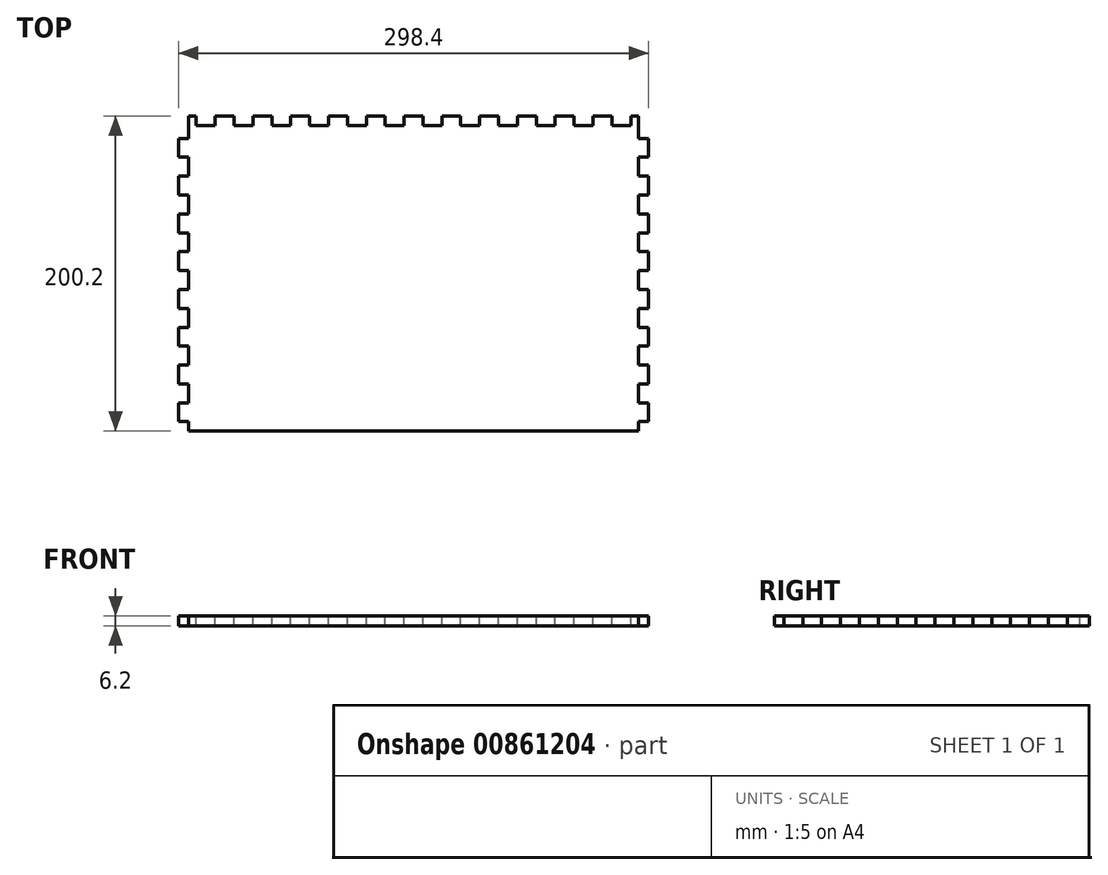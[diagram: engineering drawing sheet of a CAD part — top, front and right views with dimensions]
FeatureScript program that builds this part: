
annotation { "Feature Type Name" : "Feature", "Feature Type Description" : "" }
export const myFeature = defineFeature(function(context is Context, id is Id, definition is map)
    precondition{}
    {
        {
            var Q0;
            Q0=qCreatedBy(makeId("Top.planeOp"),FACE);
            var sketch = newSketch(context, id + "F0", { "sketchPlane" : qUnion([Q0])});
            skLineSegment(sketch, "E0.bottom", {"start": v(143, 110) * mm, "end": v(-143, 110) * mm});
            skLineSegment(sketch, "E0.top", {"start": v(143, -110) * mm, "end": v(-143, -110) * mm});
            skLineSegment(sketch, "E0.left", {"start": v(143, 110) * mm, "end": v(143, -110) * mm});
            skLineSegment(sketch, "E0.right", {"start": v(-143, 110) * mm, "end": v(-143, -110) * mm});
            skPoint(sketch, "E0.middle", {"position": v(0, 0) * mm});
            skSolve(sketch);
        }
        {
            var Q0;
            Q0=qSketchRegion(id+"F0",true);
            extrude(context, id + "F1", {"entities" : qUnion([Q0]), "depth" : 6.2 * mm, "offsetDistance" : 25 * mm});
        }
        {
            var Q0;
            Q0=makeQuery(id+"F1.opExtrude","CAP_FACE",FACE,{"disambiguationData":[OSD([sQuery(id+"F0.wireOp",EDGE,"E0.bottom"),sQuery(id+"F0.wireOp",EDGE,"E0.top"),sQuery(id+"F0.wireOp",EDGE,"E0.left"),sQuery(id+"F0.wireOp",EDGE,"E0.right")])],"isStart":false});
            var sketch = newSketch(context, id + "F2", { "sketchPlane" : qUnion([Q0])});
            skLineSegment(sketch, "E1", {"start": v(0, 110) * mm, "end": v(0, 116.2) * mm, "construction": true});
            skLineSegment(sketch, "E2.bottom", {"start": v(6, 116.2) * mm, "end": v(-6, 116.2) * mm});
            skLineSegment(sketch, "E2.top", {"start": v(6, 110) * mm, "end": v(-6, 110) * mm});
            skLineSegment(sketch, "E2.left", {"start": v(6, 116.2) * mm, "end": v(6, 110) * mm});
            skLineSegment(sketch, "E2.right", {"start": v(-6, 116.2) * mm, "end": v(-6, 110) * mm});
            skPoint(sketch, "E2.middle", {"position": v(0, 113.1) * mm});
            skLineSegment(sketch, "E3.1.0.0", {"start": v(30, 116.2) * mm, "end": v(18, 116.2) * mm});
            skLineSegment(sketch, "E3.1.0.1", {"start": v(30, 116.2) * mm, "end": v(30, 110) * mm});
            skLineSegment(sketch, "E3.1.0.2", {"start": v(18, 116.2) * mm, "end": v(18, 110) * mm});
            skLineSegment(sketch, "E3.1.0.3", {"start": v(30, 110) * mm, "end": v(18, 110) * mm});
            skLineSegment(sketch, "E3.2.0.0", {"start": v(54, 116.2) * mm, "end": v(42, 116.2) * mm});
            skLineSegment(sketch, "E3.2.0.1", {"start": v(54, 116.2) * mm, "end": v(54, 110) * mm});
            skLineSegment(sketch, "E3.2.0.2", {"start": v(42, 116.2) * mm, "end": v(42, 110) * mm});
            skLineSegment(sketch, "E3.2.0.3", {"start": v(54, 110) * mm, "end": v(42, 110) * mm});
            skLineSegment(sketch, "E3.3.0.0", {"start": v(78, 116.2) * mm, "end": v(66, 116.2) * mm});
            skLineSegment(sketch, "E3.3.0.1", {"start": v(78, 116.2) * mm, "end": v(78, 110) * mm});
            skLineSegment(sketch, "E3.3.0.2", {"start": v(66, 116.2) * mm, "end": v(66, 110) * mm});
            skLineSegment(sketch, "E3.3.0.3", {"start": v(78, 110) * mm, "end": v(66, 110) * mm});
            skLineSegment(sketch, "E3.4.0.0", {"start": v(102, 116.2) * mm, "end": v(90, 116.2) * mm});
            skLineSegment(sketch, "E3.4.0.1", {"start": v(102, 116.2) * mm, "end": v(102, 110) * mm});
            skLineSegment(sketch, "E3.4.0.2", {"start": v(90, 116.2) * mm, "end": v(90, 110) * mm});
            skLineSegment(sketch, "E3.4.0.3", {"start": v(102, 110) * mm, "end": v(90, 110) * mm});
            skLineSegment(sketch, "E3.5.0.0", {"start": v(126, 116.2) * mm, "end": v(114, 116.2) * mm});
            skLineSegment(sketch, "E3.5.0.1", {"start": v(126, 116.2) * mm, "end": v(126, 110) * mm});
            skLineSegment(sketch, "E3.5.0.2", {"start": v(114, 116.2) * mm, "end": v(114, 110) * mm});
            skLineSegment(sketch, "E3.5.0.3", {"start": v(126, 110) * mm, "end": v(114, 110) * mm});
            skLineSegment(sketch, "E3.6.0.0", {"start": v(143, 116.2) * mm, "end": v(138, 116.2) * mm});
            skLineSegment(sketch, "E3.6.0.2", {"start": v(138, 116.2) * mm, "end": v(138, 110) * mm});
            skLineSegment(sketch, "E3.6.0.3", {"start": v(143, 110) * mm, "end": v(138, 110) * mm});
            skLineSegment(sketch, "E3.direction1", {"start": v(-6, 116.2) * mm, "end": v(18, 116.2) * mm, "construction": true});
            skLineSegment(sketch, "E4", {"start": v(143, 110) * mm, "end": v(143, 116.2) * mm});
            skPoint(sketch, "E5.orphan", {"position": v(150, 110) * mm});
            skLineSegment(sketch, "E6.MirrorCS", {"start": v(-102, 110) * mm, "end": v(-90, 110) * mm});
            skLineSegment(sketch, "E7.MirrorCS", {"start": v(-143, 116.2) * mm, "end": v(-138, 116.2) * mm});
            skLineSegment(sketch, "E8.MirrorCS", {"start": v(-138, 116.2) * mm, "end": v(-138, 110) * mm});
            skLineSegment(sketch, "E9.MirrorCS", {"start": v(-30, 116.2) * mm, "end": v(-30, 110) * mm});
            skLineSegment(sketch, "E10.MirrorCS", {"start": v(-66, 116.2) * mm, "end": v(-66, 110) * mm});
            skLineSegment(sketch, "E11.MirrorCS", {"start": v(-126, 116.2) * mm, "end": v(-126, 110) * mm});
            skLineSegment(sketch, "E12.MirrorCS", {"start": v(-54, 110) * mm, "end": v(-42, 110) * mm});
            skLineSegment(sketch, "E13.MirrorCS", {"start": v(-143, 110) * mm, "end": v(-143, 116.2) * mm});
            skLineSegment(sketch, "E14.MirrorCS", {"start": v(-54, 116.2) * mm, "end": v(-54, 110) * mm});
            skLineSegment(sketch, "E15.MirrorCS", {"start": v(-114, 116.2) * mm, "end": v(-114, 110) * mm});
            skLineSegment(sketch, "E16.MirrorCS", {"start": v(-102, 116.2) * mm, "end": v(-90, 116.2) * mm});
            skLineSegment(sketch, "E17.MirrorCS", {"start": v(-102, 116.2) * mm, "end": v(-102, 110) * mm});
            skLineSegment(sketch, "E18.MirrorCS", {"start": v(-42, 116.2) * mm, "end": v(-42, 110) * mm});
            skLineSegment(sketch, "E19.MirrorCS", {"start": v(-54, 116.2) * mm, "end": v(-42, 116.2) * mm});
            skLineSegment(sketch, "E20.MirrorCS", {"start": v(-143, 110) * mm, "end": v(-138, 110) * mm});
            skLineSegment(sketch, "E21.MirrorCS", {"start": v(-90, 116.2) * mm, "end": v(-90, 110) * mm});
            skLineSegment(sketch, "E22.MirrorCS", {"start": v(-78, 116.2) * mm, "end": v(-78, 110) * mm});
            skLineSegment(sketch, "E23.MirrorCS", {"start": v(-78, 110) * mm, "end": v(-66, 110) * mm});
            skLineSegment(sketch, "E24.MirrorCS", {"start": v(-126, 116.2) * mm, "end": v(-114, 116.2) * mm});
            skLineSegment(sketch, "E25.MirrorCS", {"start": v(-78, 116.2) * mm, "end": v(-66, 116.2) * mm});
            skLineSegment(sketch, "E26.MirrorCS", {"start": v(-126, 110) * mm, "end": v(-114, 110) * mm});
            skLineSegment(sketch, "E27.MirrorCS", {"start": v(-30, 110) * mm, "end": v(-18, 110) * mm});
            skPoint(sketch, "E28.MirrorP", {"position": v(-150, 110) * mm});
            skLineSegment(sketch, "E29.MirrorCS", {"start": v(-30, 116.2) * mm, "end": v(-18, 116.2) * mm});
            skLineSegment(sketch, "E30.MirrorCS", {"start": v(-18, 116.2) * mm, "end": v(-18, 110) * mm});
            skSolve(sketch);
        }
        {
            var Q0;
            Q0=makeQuery(id+"F2.imprint","IMPRINT",FACE,{"disambiguationData":[TD([[makeQuery(id+"F2.imprint","IMPRINT",EDGE,{"derivedFrom":sQuery(id+"F2.wireOp",EDGE,"E3.6.0.0")}),1.0]])]});
            var Q1;
            Q1=makeQuery(id+"F2.imprint","IMPRINT",FACE,{"disambiguationData":[TD([[makeQuery(id+"F2.imprint","IMPRINT",EDGE,{"derivedFrom":sQuery(id+"F2.wireOp",EDGE,"E3.5.0.0")}),1.0]])]});
            var Q2;
            Q2=makeQuery(id+"F2.imprint","IMPRINT",FACE,{"disambiguationData":[TD([[makeQuery(id+"F2.imprint","IMPRINT",EDGE,{"derivedFrom":sQuery(id+"F2.wireOp",EDGE,"E3.4.0.0")}),1.0]])]});
            var Q3;
            Q3=makeQuery(id+"F2.imprint","IMPRINT",FACE,{"disambiguationData":[TD([[makeQuery(id+"F2.imprint","IMPRINT",EDGE,{"derivedFrom":sQuery(id+"F2.wireOp",EDGE,"E3.3.0.0")}),1.0]])]});
            var Q4;
            Q4=makeQuery(id+"F2.imprint","IMPRINT",FACE,{"disambiguationData":[TD([[makeQuery(id+"F2.imprint","IMPRINT",EDGE,{"derivedFrom":sQuery(id+"F2.wireOp",EDGE,"E3.2.0.0")}),1.0]])]});
            var Q5;
            Q5=makeQuery(id+"F2.imprint","IMPRINT",FACE,{"disambiguationData":[TD([[makeQuery(id+"F2.imprint","IMPRINT",EDGE,{"derivedFrom":sQuery(id+"F2.wireOp",EDGE,"E3.1.0.0")}),1.0]])]});
            var Q6;
            Q6=makeQuery(id+"F2.imprint","IMPRINT",FACE,{"disambiguationData":[TD([[makeQuery(id+"F2.imprint","IMPRINT",EDGE,{"derivedFrom":sQuery(id+"F2.wireOp",EDGE,"E2.bottom")}),1.0]])]});
            var Q7;
            Q7=makeQuery(id+"F2.imprint","IMPRINT",FACE,{"disambiguationData":[TD([[makeQuery(id+"F2.imprint","IMPRINT",EDGE,{"derivedFrom":sQuery(id+"F2.wireOp",EDGE,"E9.MirrorCS")}),1.0]])]});
            var Q8;
            Q8=makeQuery(id+"F2.imprint","IMPRINT",FACE,{"disambiguationData":[TD([[makeQuery(id+"F2.imprint","IMPRINT",EDGE,{"derivedFrom":sQuery(id+"F2.wireOp",EDGE,"E12.MirrorCS")}),-1.0]])]});
            var Q9;
            Q9=makeQuery(id+"F2.imprint","IMPRINT",FACE,{"disambiguationData":[TD([[makeQuery(id+"F2.imprint","IMPRINT",EDGE,{"derivedFrom":sQuery(id+"F2.wireOp",EDGE,"E10.MirrorCS")}),-1.0]])]});
            var Q10;
            Q10=makeQuery(id+"F2.imprint","IMPRINT",FACE,{"disambiguationData":[TD([[makeQuery(id+"F2.imprint","IMPRINT",EDGE,{"derivedFrom":sQuery(id+"F2.wireOp",EDGE,"E6.MirrorCS")}),-1.0]])]});
            var Q11;
            Q11=makeQuery(id+"F2.imprint","IMPRINT",FACE,{"disambiguationData":[TD([[makeQuery(id+"F2.imprint","IMPRINT",EDGE,{"derivedFrom":sQuery(id+"F2.wireOp",EDGE,"E11.MirrorCS")}),1.0]])]});
            var Q12;
            Q12=makeQuery(id+"F2.imprint","IMPRINT",FACE,{"disambiguationData":[TD([[makeQuery(id+"F2.imprint","IMPRINT",EDGE,{"derivedFrom":sQuery(id+"F2.wireOp",EDGE,"E7.MirrorCS")}),-1.0]])]});
            var Q13;
            Q13=makeQuery(id+"F1.opExtrude","CAP_FACE",FACE,{"disambiguationData":[OSD([sQuery(id+"F0.wireOp",EDGE,"E0.bottom"),sQuery(id+"F0.wireOp",EDGE,"E0.top"),sQuery(id+"F0.wireOp",EDGE,"E0.left"),sQuery(id+"F0.wireOp",EDGE,"E0.right")])],"isStart":true});
            extrude(context, id + "F3", {"entities" : qUnion([Q0, Q1, Q2, Q3, Q4, Q5, Q6, Q7, Q8, Q9, Q10, Q11, Q12]), "operationType" : NewBodyOperationType.ADD, "endBound" : BoundingType.UP_TO_SURFACE, "oppositeDirection" : true, "depth" : 25 * mm, "endBoundEntityFace" : qUnion([Q13]), "offsetDistance" : 25 * mm});
        }
        {
            var Q0;
            Q0=makeQuery(id+"F3.boolean.opBoolean","MERGE",FACE,{"derivedFrom":[makeQuery(id+"F1.opExtrude","CAP_FACE",FACE,{"disambiguationData":[OSD([sQuery(id+"F0.wireOp",EDGE,"E0.bottom"),sQuery(id+"F0.wireOp",EDGE,"E0.top"),sQuery(id+"F0.wireOp",EDGE,"E0.left"),sQuery(id+"F0.wireOp",EDGE,"E0.right")])],"isStart":false}),makeQuery(id+"F3.opExtrude","CAP_FACE",FACE,{"disambiguationData":[OSD([sQuery(id+"F2.wireOp",EDGE,"E2.bottom"),sQuery(id+"F2.wireOp",EDGE,"E2.top"),sQuery(id+"F2.wireOp",EDGE,"E2.left"),sQuery(id+"F2.wireOp",EDGE,"E2.right")])],"isStart":true}),makeQuery(id+"F3.opExtrude","CAP_FACE",FACE,{"disambiguationData":[OSD([sQuery(id+"F2.wireOp",EDGE,"E3.1.0.0"),sQuery(id+"F2.wireOp",EDGE,"E3.1.0.1"),sQuery(id+"F2.wireOp",EDGE,"E3.1.0.2"),sQuery(id+"F2.wireOp",EDGE,"E3.1.0.3")])],"isStart":true}),makeQuery(id+"F3.opExtrude","CAP_FACE",FACE,{"disambiguationData":[OSD([sQuery(id+"F2.wireOp",EDGE,"E3.2.0.0"),sQuery(id+"F2.wireOp",EDGE,"E3.2.0.1"),sQuery(id+"F2.wireOp",EDGE,"E3.2.0.2"),sQuery(id+"F2.wireOp",EDGE,"E3.2.0.3")])],"isStart":true}),makeQuery(id+"F3.opExtrude","CAP_FACE",FACE,{"disambiguationData":[OSD([sQuery(id+"F2.wireOp",EDGE,"E3.3.0.0"),sQuery(id+"F2.wireOp",EDGE,"E3.3.0.1"),sQuery(id+"F2.wireOp",EDGE,"E3.3.0.2"),sQuery(id+"F2.wireOp",EDGE,"E3.3.0.3")])],"isStart":true}),makeQuery(id+"F3.opExtrude","CAP_FACE",FACE,{"disambiguationData":[OSD([sQuery(id+"F2.wireOp",EDGE,"E3.4.0.0"),sQuery(id+"F2.wireOp",EDGE,"E3.4.0.1"),sQuery(id+"F2.wireOp",EDGE,"E3.4.0.2"),sQuery(id+"F2.wireOp",EDGE,"E3.4.0.3")])],"isStart":true}),makeQuery(id+"F3.opExtrude","CAP_FACE",FACE,{"disambiguationData":[OSD([sQuery(id+"F2.wireOp",EDGE,"E3.5.0.0"),sQuery(id+"F2.wireOp",EDGE,"E3.5.0.1"),sQuery(id+"F2.wireOp",EDGE,"E3.5.0.2"),sQuery(id+"F2.wireOp",EDGE,"E3.5.0.3")])],"isStart":true}),makeQuery(id+"F3.opExtrude","CAP_FACE",FACE,{"disambiguationData":[OSD([sQuery(id+"F2.wireOp",EDGE,"E3.6.0.0"),sQuery(id+"F2.wireOp",EDGE,"E3.6.0.2"),sQuery(id+"F2.wireOp",EDGE,"E3.6.0.3"),sQuery(id+"F2.wireOp",EDGE,"E4")])],"isStart":true}),makeQuery(id+"F3.opExtrude","CAP_FACE",FACE,{"disambiguationData":[OSD([sQuery(id+"F2.wireOp",EDGE,"E6.MirrorCS"),sQuery(id+"F2.wireOp",EDGE,"E16.MirrorCS"),sQuery(id+"F2.wireOp",EDGE,"E17.MirrorCS"),sQuery(id+"F2.wireOp",EDGE,"E21.MirrorCS")])],"isStart":true}),makeQuery(id+"F3.opExtrude","CAP_FACE",FACE,{"disambiguationData":[OSD([sQuery(id+"F2.wireOp",EDGE,"E7.MirrorCS"),sQuery(id+"F2.wireOp",EDGE,"E8.MirrorCS"),sQuery(id+"F2.wireOp",EDGE,"E13.MirrorCS"),sQuery(id+"F2.wireOp",EDGE,"E20.MirrorCS")])],"isStart":true}),makeQuery(id+"F3.opExtrude","CAP_FACE",FACE,{"disambiguationData":[OSD([sQuery(id+"F2.wireOp",EDGE,"E9.MirrorCS"),sQuery(id+"F2.wireOp",EDGE,"E27.MirrorCS"),sQuery(id+"F2.wireOp",EDGE,"E29.MirrorCS"),sQuery(id+"F2.wireOp",EDGE,"E30.MirrorCS")])],"isStart":true}),makeQuery(id+"F3.opExtrude","CAP_FACE",FACE,{"disambiguationData":[OSD([sQuery(id+"F2.wireOp",EDGE,"E10.MirrorCS"),sQuery(id+"F2.wireOp",EDGE,"E22.MirrorCS"),sQuery(id+"F2.wireOp",EDGE,"E23.MirrorCS"),sQuery(id+"F2.wireOp",EDGE,"E25.MirrorCS")])],"isStart":true}),makeQuery(id+"F3.opExtrude","CAP_FACE",FACE,{"disambiguationData":[OSD([sQuery(id+"F2.wireOp",EDGE,"E11.MirrorCS"),sQuery(id+"F2.wireOp",EDGE,"E15.MirrorCS"),sQuery(id+"F2.wireOp",EDGE,"E24.MirrorCS"),sQuery(id+"F2.wireOp",EDGE,"E26.MirrorCS")])],"isStart":true}),makeQuery(id+"F3.opExtrude","CAP_FACE",FACE,{"disambiguationData":[OSD([sQuery(id+"F2.wireOp",EDGE,"E12.MirrorCS"),sQuery(id+"F2.wireOp",EDGE,"E14.MirrorCS"),sQuery(id+"F2.wireOp",EDGE,"E18.MirrorCS"),sQuery(id+"F2.wireOp",EDGE,"E19.MirrorCS")])],"isStart":true})]});
            var sketch = newSketch(context, id + "F4", { "sketchPlane" : qUnion([Q0])});
            skLineSegment(sketch, "E31", {"start": v(-138, 110) * mm, "end": v(143, 110) * mm, "construction": true});
            skLineSegment(sketch, "E32", {"start": v(0, 0) * mm, "end": v(143, 0) * mm, "construction": true});
            skLineSegment(sketch, "E33", {"start": v(143, 0) * mm, "end": v(149.2, 0) * mm, "construction": true});
            skLineSegment(sketch, "E34.bottom", {"start": v(149.2, 6) * mm, "end": v(143, 6) * mm});
            skLineSegment(sketch, "E34.top", {"start": v(149.2, -6) * mm, "end": v(143, -6) * mm});
            skLineSegment(sketch, "E34.left", {"start": v(149.2, 6) * mm, "end": v(149.2, -6) * mm});
            skLineSegment(sketch, "E34.right", {"start": v(143, 6) * mm, "end": v(143, -6) * mm});
            skPoint(sketch, "E34.middle", {"position": v(146.1, 0) * mm});
            skLineSegment(sketch, "E35.0.1.0", {"start": v(149.2, 30) * mm, "end": v(143, 30) * mm});
            skLineSegment(sketch, "E35.0.1.1", {"start": v(143, 30) * mm, "end": v(143, 18) * mm});
            skLineSegment(sketch, "E35.0.1.2", {"start": v(149.2, 30) * mm, "end": v(149.2, 18) * mm});
            skLineSegment(sketch, "E35.0.1.3", {"start": v(149.2, 18) * mm, "end": v(143, 18) * mm});
            skLineSegment(sketch, "E35.0.2.0", {"start": v(149.2, 54) * mm, "end": v(143, 54) * mm});
            skLineSegment(sketch, "E35.0.2.1", {"start": v(143, 54) * mm, "end": v(143, 42) * mm});
            skLineSegment(sketch, "E35.0.2.2", {"start": v(149.2, 54) * mm, "end": v(149.2, 42) * mm});
            skLineSegment(sketch, "E35.0.2.3", {"start": v(149.2, 42) * mm, "end": v(143, 42) * mm});
            skLineSegment(sketch, "E35.0.3.0", {"start": v(149.2, 78) * mm, "end": v(143, 78) * mm});
            skLineSegment(sketch, "E35.0.3.1", {"start": v(143, 78) * mm, "end": v(143, 66) * mm});
            skLineSegment(sketch, "E35.0.3.2", {"start": v(149.2, 78) * mm, "end": v(149.2, 66) * mm});
            skLineSegment(sketch, "E35.0.3.3", {"start": v(149.2, 66) * mm, "end": v(143, 66) * mm});
            skLineSegment(sketch, "E35.0.4.0", {"start": v(149.2, 102) * mm, "end": v(143, 102) * mm});
            skLineSegment(sketch, "E35.0.4.1", {"start": v(143, 102) * mm, "end": v(143, 90) * mm});
            skLineSegment(sketch, "E35.0.4.2", {"start": v(149.2, 102) * mm, "end": v(149.2, 90) * mm});
            skLineSegment(sketch, "E35.0.4.3", {"start": v(149.2, 90) * mm, "end": v(143, 90) * mm});
            skLineSegment(sketch, "E35.direction1", {"start": v(143, 6) * mm, "end": v(168, 6) * mm, "construction": true});
            skLineSegment(sketch, "E35.direction2", {"start": v(143, 6) * mm, "end": v(143, 30) * mm, "construction": true});
            skLineSegment(sketch, "E36.MirrorCS", {"start": v(143, -30) * mm, "end": v(143, -18) * mm});
            skLineSegment(sketch, "E37.MirrorCS", {"start": v(149.2, -78) * mm, "end": v(149.2, -66) * mm});
            skLineSegment(sketch, "E38.MirrorCS", {"start": v(149.2, -66) * mm, "end": v(143, -66) * mm});
            skLineSegment(sketch, "E39.MirrorCS", {"start": v(149.2, -102) * mm, "end": v(143, -102) * mm});
            skLineSegment(sketch, "E40.MirrorCS", {"start": v(143, -102) * mm, "end": v(143, -90) * mm});
            skLineSegment(sketch, "E41.MirrorCS", {"start": v(149.2, -102) * mm, "end": v(149.2, -90) * mm});
            skLineSegment(sketch, "E42.MirrorCS", {"start": v(149.2, -90) * mm, "end": v(143, -90) * mm});
            skLineSegment(sketch, "E43.MirrorCS", {"start": v(143, -6) * mm, "end": v(143, -30) * mm, "construction": true});
            skLineSegment(sketch, "E44.MirrorCS", {"start": v(143, -54) * mm, "end": v(143, -42) * mm});
            skLineSegment(sketch, "E45.MirrorCS", {"start": v(149.2, -42) * mm, "end": v(143, -42) * mm});
            skLineSegment(sketch, "E46.MirrorCS", {"start": v(149.2, -54) * mm, "end": v(143, -54) * mm});
            skLineSegment(sketch, "E47.MirrorCS", {"start": v(149.2, -54) * mm, "end": v(149.2, -42) * mm});
            skLineSegment(sketch, "E48.MirrorCS", {"start": v(149.2, -18) * mm, "end": v(143, -18) * mm});
            skLineSegment(sketch, "E49.MirrorCS", {"start": v(143, -78) * mm, "end": v(143, -66) * mm});
            skLineSegment(sketch, "E50.MirrorCS", {"start": v(149.2, -78) * mm, "end": v(143, -78) * mm});
            skLineSegment(sketch, "E51.MirrorCS", {"start": v(149.2, -30) * mm, "end": v(143, -30) * mm});
            skLineSegment(sketch, "E52.MirrorCS", {"start": v(149.2, -30) * mm, "end": v(149.2, -18) * mm});
            skLineSegment(sketch, "E53.MirrorCS", {"start": v(-143, 6) * mm, "end": v(-143, -6) * mm});
            skLineSegment(sketch, "E54.MirrorCS", {"start": v(-149.2, 6) * mm, "end": v(-149.2, -6) * mm});
            skLineSegment(sketch, "E55.MirrorCS", {"start": v(-149.2, -6) * mm, "end": v(-143, -6) * mm});
            skLineSegment(sketch, "E56.MirrorCS", {"start": v(-149.2, 6) * mm, "end": v(-143, 6) * mm});
            skLineSegment(sketch, "E57.MirrorCS", {"start": v(-143, 0) * mm, "end": v(-149.2, 0) * mm, "construction": true});
            skLineSegment(sketch, "E58.MirrorCS", {"start": v(-143, 30) * mm, "end": v(-143, 18) * mm});
            skLineSegment(sketch, "E59.MirrorCS", {"start": v(-149.2, -30) * mm, "end": v(-143, -30) * mm});
            skLineSegment(sketch, "E60.MirrorCS", {"start": v(-143, -30) * mm, "end": v(-143, -18) * mm});
            skLineSegment(sketch, "E61.MirrorCS", {"start": v(-149.2, 30) * mm, "end": v(-143, 30) * mm});
            skLineSegment(sketch, "E62.MirrorCS", {"start": v(-149.2, 78) * mm, "end": v(-149.2, 66) * mm});
            skLineSegment(sketch, "E63.MirrorCS", {"start": v(-143, -54) * mm, "end": v(-143, -42) * mm});
            skLineSegment(sketch, "E64.MirrorCS", {"start": v(-149.2, 66) * mm, "end": v(-143, 66) * mm});
            skLineSegment(sketch, "E65.MirrorCS", {"start": v(-149.2, -42) * mm, "end": v(-143, -42) * mm});
            skLineSegment(sketch, "E66.MirrorCS", {"start": v(-149.2, 102) * mm, "end": v(-143, 102) * mm});
            skLineSegment(sketch, "E67.MirrorCS", {"start": v(-149.2, -54) * mm, "end": v(-143, -54) * mm});
            skLineSegment(sketch, "E68.MirrorCS", {"start": v(-149.2, -90) * mm, "end": v(-143, -90) * mm});
            skLineSegment(sketch, "E69.MirrorCS", {"start": v(-143, 102) * mm, "end": v(-143, 90) * mm});
            skLineSegment(sketch, "E70.MirrorCS", {"start": v(-149.2, -54) * mm, "end": v(-149.2, -42) * mm});
            skLineSegment(sketch, "E71.MirrorCS", {"start": v(-143, -102) * mm, "end": v(-143, -90) * mm});
            skLineSegment(sketch, "E72.MirrorCS", {"start": v(-149.2, 102) * mm, "end": v(-149.2, 90) * mm});
            skLineSegment(sketch, "E73.MirrorCS", {"start": v(-149.2, -18) * mm, "end": v(-143, -18) * mm});
            skLineSegment(sketch, "E74.MirrorCS", {"start": v(-149.2, -102) * mm, "end": v(-149.2, -90) * mm});
            skLineSegment(sketch, "E75.MirrorCS", {"start": v(-143, 78) * mm, "end": v(-143, 66) * mm});
            skLineSegment(sketch, "E76.MirrorCS", {"start": v(-149.2, 18) * mm, "end": v(-143, 18) * mm});
            skLineSegment(sketch, "E77.MirrorCS", {"start": v(-149.2, 42) * mm, "end": v(-143, 42) * mm});
            skLineSegment(sketch, "E78.MirrorCS", {"start": v(-149.2, -102) * mm, "end": v(-143, -102) * mm});
            skLineSegment(sketch, "E79.MirrorCS", {"start": v(-149.2, 30) * mm, "end": v(-149.2, 18) * mm});
            skLineSegment(sketch, "E80.MirrorCS", {"start": v(-149.2, -66) * mm, "end": v(-143, -66) * mm});
            skLineSegment(sketch, "E81.MirrorCS", {"start": v(-149.2, 54) * mm, "end": v(-149.2, 42) * mm});
            skLineSegment(sketch, "E82.MirrorCS", {"start": v(-149.2, -78) * mm, "end": v(-149.2, -66) * mm});
            skLineSegment(sketch, "E83.MirrorCS", {"start": v(-143, -78) * mm, "end": v(-143, -66) * mm});
            skLineSegment(sketch, "E84.MirrorCS", {"start": v(-149.2, -30) * mm, "end": v(-149.2, -18) * mm});
            skLineSegment(sketch, "E85.MirrorCS", {"start": v(-149.2, 54) * mm, "end": v(-143, 54) * mm});
            skLineSegment(sketch, "E86.MirrorCS", {"start": v(-143, -6) * mm, "end": v(-143, -30) * mm, "construction": true});
            skLineSegment(sketch, "E87.MirrorCS", {"start": v(-143, 54) * mm, "end": v(-143, 42) * mm});
            skLineSegment(sketch, "E88.MirrorCS", {"start": v(-143, 6) * mm, "end": v(-143, 30) * mm, "construction": true});
            skLineSegment(sketch, "E89.MirrorCS", {"start": v(-149.2, 78) * mm, "end": v(-143, 78) * mm});
            skLineSegment(sketch, "E90.MirrorCS", {"start": v(-149.2, -78) * mm, "end": v(-143, -78) * mm});
            skLineSegment(sketch, "E91.MirrorCS", {"start": v(-149.2, 90) * mm, "end": v(-143, 90) * mm});
            skLineSegment(sketch, "E92.MirrorCS", {"start": v(-143, 6) * mm, "end": v(-168, 6) * mm, "construction": true});
            skPoint(sketch, "E93.MirrorP", {"position": v(-146.1, 0) * mm});
            skSolve(sketch);
        }
        {
            var Q0;
            Q0=makeQuery(id+"F4.imprint","IMPRINT",FACE,{"disambiguationData":[TD([[makeQuery(id+"F4.imprint","IMPRINT",EDGE,{"derivedFrom":sQuery(id+"F4.wireOp",EDGE,"E39.MirrorCS")}),-1.0]])]});
            var Q1;
            Q1=makeQuery(id+"F4.imprint","IMPRINT",FACE,{"disambiguationData":[TD([[makeQuery(id+"F4.imprint","IMPRINT",EDGE,{"derivedFrom":sQuery(id+"F4.wireOp",EDGE,"E37.MirrorCS")}),1.0]])]});
            var Q2;
            Q2=makeQuery(id+"F4.imprint","IMPRINT",FACE,{"disambiguationData":[TD([[makeQuery(id+"F4.imprint","IMPRINT",EDGE,{"derivedFrom":sQuery(id+"F4.wireOp",EDGE,"E44.MirrorCS")}),1.0]])]});
            var Q3;
            Q3=makeQuery(id+"F4.imprint","IMPRINT",FACE,{"disambiguationData":[TD([[makeQuery(id+"F4.imprint","IMPRINT",EDGE,{"derivedFrom":sQuery(id+"F4.wireOp",EDGE,"E36.MirrorCS")}),1.0]])]});
            var Q4;
            Q4=makeQuery(id+"F4.imprint","IMPRINT",FACE,{"disambiguationData":[TD([[makeQuery(id+"F4.imprint","IMPRINT",EDGE,{"derivedFrom":sQuery(id+"F4.wireOp",EDGE,"E34.bottom")}),1.0]])]});
            var Q5;
            Q5=makeQuery(id+"F4.imprint","IMPRINT",FACE,{"disambiguationData":[TD([[makeQuery(id+"F4.imprint","IMPRINT",EDGE,{"derivedFrom":sQuery(id+"F4.wireOp",EDGE,"E35.0.1.0")}),1.0]])]});
            var Q6;
            Q6=makeQuery(id+"F4.imprint","IMPRINT",FACE,{"disambiguationData":[TD([[makeQuery(id+"F4.imprint","IMPRINT",EDGE,{"derivedFrom":sQuery(id+"F4.wireOp",EDGE,"E35.0.2.0")}),1.0]])]});
            var Q7;
            Q7=makeQuery(id+"F4.imprint","IMPRINT",FACE,{"disambiguationData":[TD([[makeQuery(id+"F4.imprint","IMPRINT",EDGE,{"derivedFrom":sQuery(id+"F4.wireOp",EDGE,"E35.0.3.0")}),1.0]])]});
            var Q8;
            Q8=makeQuery(id+"F4.imprint","IMPRINT",FACE,{"disambiguationData":[TD([[makeQuery(id+"F4.imprint","IMPRINT",EDGE,{"derivedFrom":sQuery(id+"F4.wireOp",EDGE,"E35.0.4.0")}),1.0]])]});
            var Q9;
            Q9=makeQuery(id+"F4.imprint","IMPRINT",FACE,{"disambiguationData":[TD([[makeQuery(id+"F4.imprint","IMPRINT",EDGE,{"derivedFrom":sQuery(id+"F4.wireOp",EDGE,"E66.MirrorCS")}),-1.0]])]});
            var Q10;
            Q10=makeQuery(id+"F4.imprint","IMPRINT",FACE,{"disambiguationData":[TD([[makeQuery(id+"F4.imprint","IMPRINT",EDGE,{"derivedFrom":sQuery(id+"F4.wireOp",EDGE,"E62.MirrorCS")}),1.0]])]});
            var Q11;
            Q11=makeQuery(id+"F4.imprint","IMPRINT",FACE,{"disambiguationData":[TD([[makeQuery(id+"F4.imprint","IMPRINT",EDGE,{"derivedFrom":sQuery(id+"F4.wireOp",EDGE,"E77.MirrorCS")}),1.0]])]});
            var Q12;
            Q12=makeQuery(id+"F4.imprint","IMPRINT",FACE,{"disambiguationData":[TD([[makeQuery(id+"F4.imprint","IMPRINT",EDGE,{"derivedFrom":sQuery(id+"F4.wireOp",EDGE,"E58.MirrorCS")}),-1.0]])]});
            var Q13;
            Q13=makeQuery(id+"F4.imprint","IMPRINT",FACE,{"disambiguationData":[TD([[makeQuery(id+"F4.imprint","IMPRINT",EDGE,{"derivedFrom":sQuery(id+"F4.wireOp",EDGE,"E53.MirrorCS")}),-1.0]])]});
            var Q14;
            Q14=makeQuery(id+"F4.imprint","IMPRINT",FACE,{"disambiguationData":[TD([[makeQuery(id+"F4.imprint","IMPRINT",EDGE,{"derivedFrom":sQuery(id+"F4.wireOp",EDGE,"E59.MirrorCS")}),1.0]])]});
            var Q15;
            Q15=makeQuery(id+"F4.imprint","IMPRINT",FACE,{"disambiguationData":[TD([[makeQuery(id+"F4.imprint","IMPRINT",EDGE,{"derivedFrom":sQuery(id+"F4.wireOp",EDGE,"E63.MirrorCS")}),-1.0]])]});
            var Q16;
            Q16=makeQuery(id+"F4.imprint","IMPRINT",FACE,{"disambiguationData":[TD([[makeQuery(id+"F4.imprint","IMPRINT",EDGE,{"derivedFrom":sQuery(id+"F4.wireOp",EDGE,"E80.MirrorCS")}),-1.0]])]});
            var Q17;
            Q17=makeQuery(id+"F4.imprint","IMPRINT",FACE,{"disambiguationData":[TD([[makeQuery(id+"F4.imprint","IMPRINT",EDGE,{"derivedFrom":sQuery(id+"F4.wireOp",EDGE,"E68.MirrorCS")}),-1.0]])]});
            var Q18;
            {var subQ0=sQuery(id+"F0.wireOp",EDGE,"E0.right");var subQ1=sQuery(id+"F0.wireOp",EDGE,"E0.left");var subQ2=sQuery(id+"F0.wireOp",EDGE,"E0.top");var subQ3=sQuery(id+"F0.wireOp",EDGE,"E0.bottom");Q18=makeQuery(id+"F3.boolean.opBoolean","MERGE",FACE,{"derivedFrom":[makeQuery(id+"F1.opExtrude","CAP_FACE",FACE,{"disambiguationData":[OSD([subQ3,subQ2,subQ1,subQ0])],"isStart":true}),makeQuery(id+"F3.opExtrude","CAP_FACE",FACE,{"disambiguationData":[OSD([subQ3,subQ2,subQ1,subQ0]),OD(0.0)],"isStart":false}),makeQuery(id+"F3.opExtrude","CAP_FACE",FACE,{"disambiguationData":[OSD([subQ3,subQ2,subQ1,subQ0]),OD(1.0)],"isStart":false}),makeQuery(id+"F3.opExtrude","CAP_FACE",FACE,{"disambiguationData":[OSD([subQ3,subQ2,subQ1,subQ0]),OD(2.0)],"isStart":false}),makeQuery(id+"F3.opExtrude","CAP_FACE",FACE,{"disambiguationData":[OSD([subQ3,subQ2,subQ1,subQ0]),OD(3.0)],"isStart":false}),makeQuery(id+"F3.opExtrude","CAP_FACE",FACE,{"disambiguationData":[OSD([subQ3,subQ2,subQ1,subQ0]),OD(4.0)],"isStart":false}),makeQuery(id+"F3.opExtrude","CAP_FACE",FACE,{"disambiguationData":[OSD([subQ3,subQ2,subQ1,subQ0]),OD(5.0)],"isStart":false}),makeQuery(id+"F3.opExtrude","CAP_FACE",FACE,{"disambiguationData":[OSD([subQ3,subQ2,subQ1,subQ0]),OD(6.0)],"isStart":false}),makeQuery(id+"F3.opExtrude","CAP_FACE",FACE,{"disambiguationData":[OSD([subQ3,subQ2,subQ1,subQ0]),OD(7.0)],"isStart":false}),makeQuery(id+"F3.opExtrude","CAP_FACE",FACE,{"disambiguationData":[OSD([subQ3,subQ2,subQ1,subQ0]),OD(8.0)],"isStart":false}),makeQuery(id+"F3.opExtrude","CAP_FACE",FACE,{"disambiguationData":[OSD([subQ3,subQ2,subQ1,subQ0]),OD(9.0)],"isStart":false}),makeQuery(id+"F3.opExtrude","CAP_FACE",FACE,{"disambiguationData":[OSD([subQ3,subQ2,subQ1,subQ0]),OD(10.0)],"isStart":false}),makeQuery(id+"F3.opExtrude","CAP_FACE",FACE,{"disambiguationData":[OSD([subQ3,subQ2,subQ1,subQ0]),OD(11.0)],"isStart":false}),makeQuery(id+"F3.opExtrude","CAP_FACE",FACE,{"disambiguationData":[OSD([subQ3,subQ2,subQ1,subQ0]),OD(12.0)],"isStart":false})]});}
            extrude(context, id + "F5", {"entities" : qUnion([Q0, Q1, Q2, Q3, Q4, Q5, Q6, Q7, Q8, Q9, Q10, Q11, Q12, Q13, Q14, Q15, Q16, Q17]), "operationType" : NewBodyOperationType.ADD, "endBound" : BoundingType.UP_TO_SURFACE, "oppositeDirection" : true, "depth" : 25 * mm, "endBoundEntityFace" : qUnion([Q18]), "offsetDistance" : 25 * mm});
        }
        {
            var Q0;
            Q0=makeQuery(id+"F5.boolean.opBoolean","MERGE",FACE,{"derivedFrom":[makeQuery(id+"F3.boolean.opBoolean","MERGE",FACE,{"derivedFrom":[makeQuery(id+"F1.opExtrude","CAP_FACE",FACE,{"disambiguationData":[OSD([sQuery(id+"F0.wireOp",EDGE,"E0.bottom"),sQuery(id+"F0.wireOp",EDGE,"E0.top"),sQuery(id+"F0.wireOp",EDGE,"E0.left"),sQuery(id+"F0.wireOp",EDGE,"E0.right")])],"isStart":false}),makeQuery(id+"F3.opExtrude","CAP_FACE",FACE,{"disambiguationData":[OSD([sQuery(id+"F2.wireOp",EDGE,"E2.bottom"),sQuery(id+"F2.wireOp",EDGE,"E2.top"),sQuery(id+"F2.wireOp",EDGE,"E2.left"),sQuery(id+"F2.wireOp",EDGE,"E2.right")])],"isStart":true}),makeQuery(id+"F3.opExtrude","CAP_FACE",FACE,{"disambiguationData":[OSD([sQuery(id+"F2.wireOp",EDGE,"E3.1.0.0"),sQuery(id+"F2.wireOp",EDGE,"E3.1.0.1"),sQuery(id+"F2.wireOp",EDGE,"E3.1.0.2"),sQuery(id+"F2.wireOp",EDGE,"E3.1.0.3")])],"isStart":true}),makeQuery(id+"F3.opExtrude","CAP_FACE",FACE,{"disambiguationData":[OSD([sQuery(id+"F2.wireOp",EDGE,"E3.2.0.0"),sQuery(id+"F2.wireOp",EDGE,"E3.2.0.1"),sQuery(id+"F2.wireOp",EDGE,"E3.2.0.2"),sQuery(id+"F2.wireOp",EDGE,"E3.2.0.3")])],"isStart":true}),makeQuery(id+"F3.opExtrude","CAP_FACE",FACE,{"disambiguationData":[OSD([sQuery(id+"F2.wireOp",EDGE,"E3.3.0.0"),sQuery(id+"F2.wireOp",EDGE,"E3.3.0.1"),sQuery(id+"F2.wireOp",EDGE,"E3.3.0.2"),sQuery(id+"F2.wireOp",EDGE,"E3.3.0.3")])],"isStart":true}),makeQuery(id+"F3.opExtrude","CAP_FACE",FACE,{"disambiguationData":[OSD([sQuery(id+"F2.wireOp",EDGE,"E3.4.0.0"),sQuery(id+"F2.wireOp",EDGE,"E3.4.0.1"),sQuery(id+"F2.wireOp",EDGE,"E3.4.0.2"),sQuery(id+"F2.wireOp",EDGE,"E3.4.0.3")])],"isStart":true}),makeQuery(id+"F3.opExtrude","CAP_FACE",FACE,{"disambiguationData":[OSD([sQuery(id+"F2.wireOp",EDGE,"E3.5.0.0"),sQuery(id+"F2.wireOp",EDGE,"E3.5.0.1"),sQuery(id+"F2.wireOp",EDGE,"E3.5.0.2"),sQuery(id+"F2.wireOp",EDGE,"E3.5.0.3")])],"isStart":true}),makeQuery(id+"F3.opExtrude","CAP_FACE",FACE,{"disambiguationData":[OSD([sQuery(id+"F2.wireOp",EDGE,"E3.6.0.0"),sQuery(id+"F2.wireOp",EDGE,"E3.6.0.2"),sQuery(id+"F2.wireOp",EDGE,"E3.6.0.3"),sQuery(id+"F2.wireOp",EDGE,"E4")])],"isStart":true}),makeQuery(id+"F3.opExtrude","CAP_FACE",FACE,{"disambiguationData":[OSD([sQuery(id+"F2.wireOp",EDGE,"E6.MirrorCS"),sQuery(id+"F2.wireOp",EDGE,"E16.MirrorCS"),sQuery(id+"F2.wireOp",EDGE,"E17.MirrorCS"),sQuery(id+"F2.wireOp",EDGE,"E21.MirrorCS")])],"isStart":true}),makeQuery(id+"F3.opExtrude","CAP_FACE",FACE,{"disambiguationData":[OSD([sQuery(id+"F2.wireOp",EDGE,"E7.MirrorCS"),sQuery(id+"F2.wireOp",EDGE,"E8.MirrorCS"),sQuery(id+"F2.wireOp",EDGE,"E13.MirrorCS"),sQuery(id+"F2.wireOp",EDGE,"E20.MirrorCS")])],"isStart":true}),makeQuery(id+"F3.opExtrude","CAP_FACE",FACE,{"disambiguationData":[OSD([sQuery(id+"F2.wireOp",EDGE,"E9.MirrorCS"),sQuery(id+"F2.wireOp",EDGE,"E27.MirrorCS"),sQuery(id+"F2.wireOp",EDGE,"E29.MirrorCS"),sQuery(id+"F2.wireOp",EDGE,"E30.MirrorCS")])],"isStart":true}),makeQuery(id+"F3.opExtrude","CAP_FACE",FACE,{"disambiguationData":[OSD([sQuery(id+"F2.wireOp",EDGE,"E10.MirrorCS"),sQuery(id+"F2.wireOp",EDGE,"E22.MirrorCS"),sQuery(id+"F2.wireOp",EDGE,"E23.MirrorCS"),sQuery(id+"F2.wireOp",EDGE,"E25.MirrorCS")])],"isStart":true}),makeQuery(id+"F3.opExtrude","CAP_FACE",FACE,{"disambiguationData":[OSD([sQuery(id+"F2.wireOp",EDGE,"E11.MirrorCS"),sQuery(id+"F2.wireOp",EDGE,"E15.MirrorCS"),sQuery(id+"F2.wireOp",EDGE,"E24.MirrorCS"),sQuery(id+"F2.wireOp",EDGE,"E26.MirrorCS")])],"isStart":true}),makeQuery(id+"F3.opExtrude","CAP_FACE",FACE,{"disambiguationData":[OSD([sQuery(id+"F2.wireOp",EDGE,"E12.MirrorCS"),sQuery(id+"F2.wireOp",EDGE,"E14.MirrorCS"),sQuery(id+"F2.wireOp",EDGE,"E18.MirrorCS"),sQuery(id+"F2.wireOp",EDGE,"E19.MirrorCS")])],"isStart":true})]}),makeQuery(id+"F5.opExtrude","CAP_FACE",FACE,{"disambiguationData":[OSD([sQuery(id+"F4.wireOp",EDGE,"E34.bottom"),sQuery(id+"F4.wireOp",EDGE,"E34.top"),sQuery(id+"F4.wireOp",EDGE,"E34.left"),sQuery(id+"F4.wireOp",EDGE,"E34.right")])],"isStart":true}),makeQuery(id+"F5.opExtrude","CAP_FACE",FACE,{"disambiguationData":[OSD([sQuery(id+"F4.wireOp",EDGE,"E35.0.1.0"),sQuery(id+"F4.wireOp",EDGE,"E35.0.1.1"),sQuery(id+"F4.wireOp",EDGE,"E35.0.1.2"),sQuery(id+"F4.wireOp",EDGE,"E35.0.1.3")])],"isStart":true}),makeQuery(id+"F5.opExtrude","CAP_FACE",FACE,{"disambiguationData":[OSD([sQuery(id+"F4.wireOp",EDGE,"E35.0.2.0"),sQuery(id+"F4.wireOp",EDGE,"E35.0.2.1"),sQuery(id+"F4.wireOp",EDGE,"E35.0.2.2"),sQuery(id+"F4.wireOp",EDGE,"E35.0.2.3")])],"isStart":true}),makeQuery(id+"F5.opExtrude","CAP_FACE",FACE,{"disambiguationData":[OSD([sQuery(id+"F4.wireOp",EDGE,"E35.0.3.0"),sQuery(id+"F4.wireOp",EDGE,"E35.0.3.1"),sQuery(id+"F4.wireOp",EDGE,"E35.0.3.2"),sQuery(id+"F4.wireOp",EDGE,"E35.0.3.3")])],"isStart":true}),makeQuery(id+"F5.opExtrude","CAP_FACE",FACE,{"disambiguationData":[OSD([sQuery(id+"F4.wireOp",EDGE,"E35.0.4.0"),sQuery(id+"F4.wireOp",EDGE,"E35.0.4.1"),sQuery(id+"F4.wireOp",EDGE,"E35.0.4.2"),sQuery(id+"F4.wireOp",EDGE,"E35.0.4.3")])],"isStart":true}),makeQuery(id+"F5.opExtrude","CAP_FACE",FACE,{"disambiguationData":[OSD([sQuery(id+"F4.wireOp",EDGE,"E36.MirrorCS"),sQuery(id+"F4.wireOp",EDGE,"E48.MirrorCS"),sQuery(id+"F4.wireOp",EDGE,"E51.MirrorCS"),sQuery(id+"F4.wireOp",EDGE,"E52.MirrorCS")])],"isStart":true}),makeQuery(id+"F5.opExtrude","CAP_FACE",FACE,{"disambiguationData":[OSD([sQuery(id+"F4.wireOp",EDGE,"E37.MirrorCS"),sQuery(id+"F4.wireOp",EDGE,"E38.MirrorCS"),sQuery(id+"F4.wireOp",EDGE,"E49.MirrorCS"),sQuery(id+"F4.wireOp",EDGE,"E50.MirrorCS")])],"isStart":true}),makeQuery(id+"F5.opExtrude","CAP_FACE",FACE,{"disambiguationData":[OSD([sQuery(id+"F4.wireOp",EDGE,"E39.MirrorCS"),sQuery(id+"F4.wireOp",EDGE,"E40.MirrorCS"),sQuery(id+"F4.wireOp",EDGE,"E41.MirrorCS"),sQuery(id+"F4.wireOp",EDGE,"E42.MirrorCS")])],"isStart":true}),makeQuery(id+"F5.opExtrude","CAP_FACE",FACE,{"disambiguationData":[OSD([sQuery(id+"F4.wireOp",EDGE,"E44.MirrorCS"),sQuery(id+"F4.wireOp",EDGE,"E45.MirrorCS"),sQuery(id+"F4.wireOp",EDGE,"E46.MirrorCS"),sQuery(id+"F4.wireOp",EDGE,"E47.MirrorCS")])],"isStart":true}),makeQuery(id+"F5.opExtrude","CAP_FACE",FACE,{"disambiguationData":[OSD([sQuery(id+"F4.wireOp",EDGE,"E53.MirrorCS"),sQuery(id+"F4.wireOp",EDGE,"E54.MirrorCS"),sQuery(id+"F4.wireOp",EDGE,"E55.MirrorCS"),sQuery(id+"F4.wireOp",EDGE,"E56.MirrorCS")])],"isStart":true}),makeQuery(id+"F5.opExtrude","CAP_FACE",FACE,{"disambiguationData":[OSD([sQuery(id+"F4.wireOp",EDGE,"E58.MirrorCS"),sQuery(id+"F4.wireOp",EDGE,"E61.MirrorCS"),sQuery(id+"F4.wireOp",EDGE,"E76.MirrorCS"),sQuery(id+"F4.wireOp",EDGE,"E79.MirrorCS")])],"isStart":true}),makeQuery(id+"F5.opExtrude","CAP_FACE",FACE,{"disambiguationData":[OSD([sQuery(id+"F4.wireOp",EDGE,"E59.MirrorCS"),sQuery(id+"F4.wireOp",EDGE,"E60.MirrorCS"),sQuery(id+"F4.wireOp",EDGE,"E73.MirrorCS"),sQuery(id+"F4.wireOp",EDGE,"E84.MirrorCS")])],"isStart":true}),makeQuery(id+"F5.opExtrude","CAP_FACE",FACE,{"disambiguationData":[OSD([sQuery(id+"F4.wireOp",EDGE,"E62.MirrorCS"),sQuery(id+"F4.wireOp",EDGE,"E64.MirrorCS"),sQuery(id+"F4.wireOp",EDGE,"E75.MirrorCS"),sQuery(id+"F4.wireOp",EDGE,"E89.MirrorCS")])],"isStart":true}),makeQuery(id+"F5.opExtrude","CAP_FACE",FACE,{"disambiguationData":[OSD([sQuery(id+"F4.wireOp",EDGE,"E63.MirrorCS"),sQuery(id+"F4.wireOp",EDGE,"E65.MirrorCS"),sQuery(id+"F4.wireOp",EDGE,"E67.MirrorCS"),sQuery(id+"F4.wireOp",EDGE,"E70.MirrorCS")])],"isStart":true}),makeQuery(id+"F5.opExtrude","CAP_FACE",FACE,{"disambiguationData":[OSD([sQuery(id+"F4.wireOp",EDGE,"E66.MirrorCS"),sQuery(id+"F4.wireOp",EDGE,"E69.MirrorCS"),sQuery(id+"F4.wireOp",EDGE,"E72.MirrorCS"),sQuery(id+"F4.wireOp",EDGE,"E91.MirrorCS")])],"isStart":true}),makeQuery(id+"F5.opExtrude","CAP_FACE",FACE,{"disambiguationData":[OSD([sQuery(id+"F4.wireOp",EDGE,"E68.MirrorCS"),sQuery(id+"F4.wireOp",EDGE,"E71.MirrorCS"),sQuery(id+"F4.wireOp",EDGE,"E74.MirrorCS"),sQuery(id+"F4.wireOp",EDGE,"E78.MirrorCS")])],"isStart":true}),makeQuery(id+"F5.opExtrude","CAP_FACE",FACE,{"disambiguationData":[OSD([sQuery(id+"F4.wireOp",EDGE,"E77.MirrorCS"),sQuery(id+"F4.wireOp",EDGE,"E81.MirrorCS"),sQuery(id+"F4.wireOp",EDGE,"E85.MirrorCS"),sQuery(id+"F4.wireOp",EDGE,"E87.MirrorCS")])],"isStart":true}),makeQuery(id+"F5.opExtrude","CAP_FACE",FACE,{"disambiguationData":[OSD([sQuery(id+"F4.wireOp",EDGE,"E80.MirrorCS"),sQuery(id+"F4.wireOp",EDGE,"E82.MirrorCS"),sQuery(id+"F4.wireOp",EDGE,"E83.MirrorCS"),sQuery(id+"F4.wireOp",EDGE,"E90.MirrorCS")])],"isStart":true})]});
            var sketch = newSketch(context, id + "F6", { "sketchPlane" : qUnion([Q0])});
            skLineSegment(sketch, "E94", {"start": v(-143, -110) * mm, "end": v(-149.2, -110) * mm, "construction": true});
            skLineSegment(sketch, "E95.bottom", {"start": v(-149.2, -110) * mm, "end": v(180.47, -110) * mm});
            skLineSegment(sketch, "E95.top", {"start": v(-149.2, -84) * mm, "end": v(180.47, -84) * mm});
            skLineSegment(sketch, "E95.left", {"start": v(-149.2, -110) * mm, "end": v(-149.2, -84) * mm});
            skLineSegment(sketch, "E95.right", {"start": v(180.47, -110) * mm, "end": v(180.47, -84) * mm});
            skSolve(sketch);
        }
        {
            var Q0;
            Q0 = qSketchRegion(id + "F6", true);
            extrude(context, id + "F7", {"entities" : qUnion([Q0]), "operationType" : NewBodyOperationType.REMOVE, "endBound" : BoundingType.THROUGH_ALL, "oppositeDirection" : true, "depth" : 25 * mm, "offsetDistance" : 25 * mm});
        }
    });
